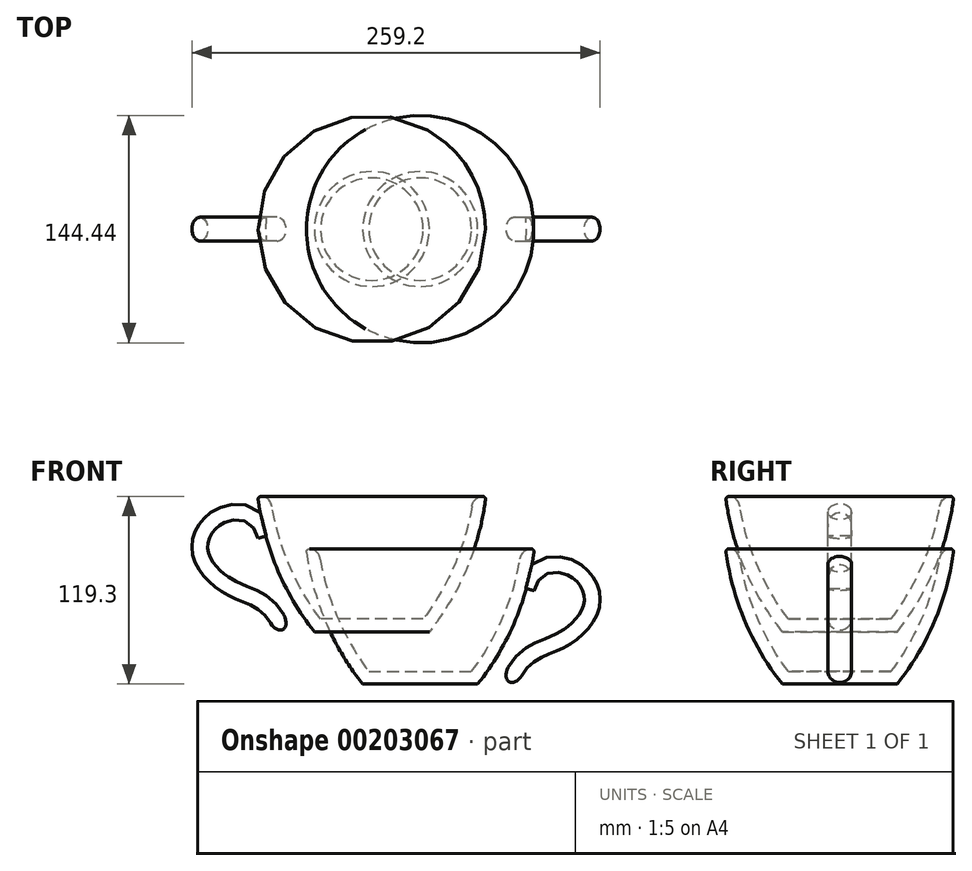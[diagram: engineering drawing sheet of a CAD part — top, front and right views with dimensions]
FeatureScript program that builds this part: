
annotation { "Feature Type Name" : "Feature", "Feature Type Description" : "" }
export const myFeature = defineFeature(function(context is Context, id is Id, definition is map)
    precondition{}
    {
        {
            var Q0;
            Q0=qCreatedBy(makeId("Top.planeOp"),FACE);
            var sketch = newSketch(context, id + "F0", { "sketchPlane" : qUnion([Q0])});
            skLineSegment(sketch, "E0", {"start": v(0, 65.57) * mm, "end": v(0, -66.94) * mm, "construction": true});
            skSolve(sketch);
        }
        {
            var Q0;
            Q0=qCreatedBy(makeId("Front.planeOp"),FACE);
            var sketch = newSketch(context, id + "F1", { "sketchPlane" : qUnion([Q0])});
            skLineSegment(sketch, "E1", {"start": v(-32.58, 0) * mm, "end": v(0, 0) * mm});
            skLineSegment(sketch, "E2", {"start": v(-36.5, -8) * mm, "end": v(0, -8) * mm});
            skLineSegment(sketch, "E3", {"start": v(0, 0) * mm, "end": v(0, -8) * mm});
            skArc(sketch, "E4", {"start": v(-72.2, 75.73) * mm, "mid": v(-59.99, 31.46) * mm, "end": v(-36.5, -8) * mm});
            skArc(sketch, "E5", {"start": v(-63.47, 71.55) * mm, "mid": v(-52.33, 33.91) * mm, "end": v(-32.58, 0) * mm});
            skLineSegment(sketch, "E6", {"start": v(-32.58, 0) * mm, "end": v(-38.96, -4.82) * mm, "construction": true});
            skLineSegment(sketch, "E7", {"start": v(-25.94, -8.79) * mm, "end": v(-39.22, 8.79) * mm, "construction": true});
            skPoint(sketch, "E8.visualSharp", {"position": v(-72.5, 78) * mm});
            skArc(sketch, "E8.filletArc", {"start": v(-70.22, 78) * mm, "mid": v(-71.73, 77.32) * mm, "end": v(-72.2, 75.73) * mm});
            skEllipticalArc(sketch, "E9", {});
            skLineSegment(sketch, "E10", {"start": v(-72.5, 78) * mm, "end": v(-61.94, -8) * mm, "construction": true});
            skLineSegment(sketch, "E11", {"start": v(-70.22, 78) * mm, "end": v(-70.22, 76) * mm, "construction": true});
            skLineSegment(sketch, "E12", {"start": v(-70.22, 70) * mm, "end": v(-70.22, 76) * mm, "construction": true});
            skLineSegment(sketch, "E13.MirrorCS", {"start": v(32.58, 0) * mm, "end": v(0, 0) * mm});
            skLineSegment(sketch, "E14.MirrorCS", {"start": v(36.5, -8) * mm, "end": v(0, -8) * mm});
            skArc(sketch, "E15.MirrorCS", {"start": v(72.2, 75.73) * mm, "mid": v(59.99, 31.46) * mm, "end": v(36.5, -8) * mm});
            skArc(sketch, "E16.MirrorCS", {"start": v(63.47, 71.55) * mm, "mid": v(52.33, 33.91) * mm, "end": v(32.58, 0) * mm});
            skEllipticalArc(sketch, "E17.MirrorCS", {});
            skArc(sketch, "E18.MirrorCS", {"start": v(70.22, 78) * mm, "mid": v(71.73, 77.32) * mm, "end": v(72.2, 75.73) * mm});
            skEllipticalArc(sketch, "E19.1.0", {});
            skArc(sketch, "E19.1.1", {"start": v(-62.5, 17.79) * mm, "mid": v(-37.88, -20.98) * mm, "end": v(-3.88, -51.85) * mm});
            skArc(sketch, "E19.1.2", {"start": v(-52.94, 16.34) * mm, "mid": v(-31.28, -16.4) * mm, "end": v(-2.47, -43.05) * mm});
            skArc(sketch, "E19.1.3", {"start": v(-61.28, 20.54) * mm, "mid": v(-62.52, 19.44) * mm, "end": v(-62.5, 17.79) * mm});
            skEllipticalArc(sketch, "E19.1.4", {});
            skArc(sketch, "E19.1.5", {"start": v(73.03, 61.6) * mm, "mid": v(74.68, 61.38) * mm, "end": v(75.6, 60) * mm});
            skArc(sketch, "E19.1.6", {"start": v(75.6, 60) * mm, "mid": v(76.85, 14.1) * mm, "end": v(65.93, -30.5) * mm});
            skArc(sketch, "E19.1.7", {"start": v(68.47, 53.45) * mm, "mid": v(68.82, 14.2) * mm, "end": v(59.84, -24) * mm});
            skLineSegment(sketch, "E19.1.8", {"start": v(59.84, -24) * mm, "end": v(28.68, -33.52) * mm});
            skLineSegment(sketch, "E19.1.9", {"start": v(65.93, -30.5) * mm, "end": v(31.02, -41.17) * mm});
            skLineSegment(sketch, "E19.1.10", {"start": v(-2.47, -43.05) * mm, "end": v(28.68, -33.52) * mm});
            skLineSegment(sketch, "E19.1.11", {"start": v(-3.88, -51.85) * mm, "end": v(31.02, -41.17) * mm});
            skPoint(sketch, "E19.center", {"position": v(126.5, 79.2) * mm});
            skLineSegment(sketch, "E19.anchor1", {"start": v(126.5, 79.2) * mm, "end": v(-70.22, 70) * mm, "construction": true});
            skLineSegment(sketch, "E19.anchor2", {"start": v(126.5, 79.2) * mm, "end": v(-58.94, 12.89) * mm, "construction": true});
            const initialGuessF1  = {"E9": [-0.07022425278979688, 0.07, 0, 1, 0.008, 0.0068794865450414, 4.9070171506327815, 0], "E17.MirrorCS": [0.07022425278979687, 0.07, 0, 1, 0.008, 0.0068794865450414, 0, 1.3761681565468047], "E19.1.0": [-0.058938518872708, 0.012885391096680493, -0.29237170472273716, 0.9563047559630353, 0.008, 0.0068794865450414, 4.9070171506327815, 0], "E19.1.4": [0.0753730549809584, 0.053948560098747184, -0.29237170472273716, 0.9563047559630353, 0.008, 0.0068794865450414, 0, 1.376168156546805]};
            skSetInitialGuess(sketch, initialGuessF1);
            skSolve(sketch);
        }
        {
            var Q0;
            Q0=qCreatedBy(makeId("Front.planeOp"),FACE);
            var sketch = newSketch(context, id + "F2", { "sketchPlane" : qUnion([Q0])});
            skFitSpline(sketch, "E20", {"points": [v(-60.2, 0) * mm, v(-87.86, 19.08) * mm, v(-108.8, 41.65) * mm, v(-97.89, 64.66) * mm, v(-67.44, 52.68) * mm], "startDerivative": vector(-89.07, 152.6) * mm, "endDerivative": vector(57.78, -206.9) * mm});
            skLineSegment(sketch, "E21", {"start": v(-55.87, 2.52) * mm, "end": v(-64.5, -2.52) * mm});
            skLineSegment(sketch, "E22", {"start": v(-60.2, 0) * mm, "end": v(-80.7, 35.14) * mm, "construction": true});
            skLineSegment(sketch, "E23", {"start": v(-35.9, -29.37) * mm, "end": v(-73.82, 35.6) * mm, "construction": true});
            skLineSegment(sketch, "E24", {"start": v(-55.87, 2.52) * mm, "end": v(-54.86, 3.11) * mm, "construction": true});
            skLineSegment(sketch, "E25", {"start": v(-70.87, 64.96) * mm, "end": v(-64, 40.4) * mm, "construction": true});
            skSolve(sketch);
        }
        {
            var Q0;
            Q0=sQuery(id+"F2.wireOp",EDGE,"E21");
            cPlane(context, id + "F3", {"entities" : qUnion([Q0]), "cplaneType" : CPlaneType.LINE_ANGLE, "offset" : 25 * mm, "angle" : 90 * degree, "width" : 150 * mm, "height" : 150 * mm});
        }
        {
            var Q0;
            Q0=qCreatedBy(id+"F3.planeOp",FACE);
            var sketch = newSketch(context, id + "F4", { "sketchPlane" : qUnion([Q0])});
            skEllipse(sketch, "E26", {"center": v(-51.98, 0) * mm, "majorRadius": 5 * mm, "minorRadius": 7.5 * mm, "majorAxis": v(-1, 0)});
            skLineSegment(sketch, "E27", {"start": v(-51.98, 0) * mm, "end": v(-46.98, 0) * mm, "construction": true});
            skLineSegment(sketch, "E28", {"start": v(-51.98, 0) * mm, "end": v(-51.98, -7.5) * mm, "construction": true});
            skLineSegment(sketch, "E29", {"start": v(-46.98, 0) * mm, "end": v(-56.98, 0) * mm});
            skSolve(sketch);
        }
        {
            var Q0;
            Q0=makeQuery(id+"F1.imprint","IMPRINT",FACE,{"disambiguationData":[TD([[makeQuery(id+"F1.imprint","IMPRINT",EDGE,{"derivedFrom":sQuery(id+"F1.wireOp",EDGE,"E1")}),-1.0]])]});
            var Q1;
            Q1=sQuery(id+"F1.wireOp",EDGE,"E3");
            revolve(context, id + "F5", {"entities" : qUnion([Q0]), "axis" : qUnion([Q1]), "revolveType" : RevolveType.FULL});
        }
        {
            var Q0;
            Q0=makeQuery(id+"F4.imprint","IMPRINT",FACE,{"disambiguationData":[TD([[makeQuery(id+"F4.imprint","IMPRINT",EDGE,{"derivedFrom":sQuery(id+"F4.wireOp",EDGE,"E26")}),1.0]])]});
            var Q1;
            Q1=sQuery(id+"F2.wireOp",EDGE,"E20");
            sweep(context, id + "F6", {"operationType" : NewBodyOperationType.ADD, "profiles" : qUnion([Q0]), "path" : qUnion([Q1])});
        }
        {
            var Q0;
            {var subQ0=sQuery(id+"F4.wireOp",EDGE,"E29");Q0=makeQuery(id+"F4.imprint","IMPRINT",FACE,{"disambiguationData":[TD([[makeQuery(id+"F4.imprint","IMPRINT",EDGE,{"derivedFrom":subQ0}),1.0]])]});}
            var Q1;
            Q1=sQuery(id+"F4.wireOp",EDGE,"E29");
            revolve(context, id + "F7", {"operationType" : NewBodyOperationType.ADD, "entities" : qUnion([Q0]), "axis" : qUnion([Q1]), "revolveType" : RevolveType.FULL});
        }
        {
            var Q0;
            Q0=makeQuery(id+"F5.opRevolve","SWEPT_BODY",BODY,{"disambiguationData":[OSD([sQuery(id+"F1.wireOp",EDGE,"E1"),sQuery(id+"F1.wireOp",EDGE,"E2"),sQuery(id+"F1.wireOp",EDGE,"E3"),sQuery(id+"F1.wireOp",EDGE,"E4"),sQuery(id+"F1.wireOp",EDGE,"E5"),sQuery(id+"F1.wireOp",EDGE,"E8.filletArc"),sQuery(id+"F1.wireOp",EDGE,"E9")])]});
            var Q1;
            Q1=sQuery(id+"F1.wireOp",EDGE,"E3");
            transform(context, id + "F8", {"entities" : qUnion([Q0]), "transformType" : TransformType.ROTATION, "transformAxis" : qUnion([Q1]), "angle" : 180 * degree, "makeCopy" : true});
        }
        {
            var Q0;
            Q0=makeQuery(id+"F8.opPattern","COPY",BODY,{"derivedFrom":makeQuery(id+"F5.opRevolve","SWEPT_BODY",BODY,{"disambiguationData":[OSD([sQuery(id+"F1.wireOp",EDGE,"E1"),sQuery(id+"F1.wireOp",EDGE,"E2"),sQuery(id+"F1.wireOp",EDGE,"E3"),sQuery(id+"F1.wireOp",EDGE,"E4"),sQuery(id+"F1.wireOp",EDGE,"E5"),sQuery(id+"F1.wireOp",EDGE,"E8.filletArc"),sQuery(id+"F1.wireOp",EDGE,"E9")])]}),"instanceName":"1"});
            transform(context, id + "F9", {"entities" : qUnion([Q0]), "transformType" : TransformType.TRANSLATION_3D, "dx" : 30.7 * mm, "dy" : 0 * mm, "dz" : -33.3 * mm, "makeCopy" : false});
        }
    });
